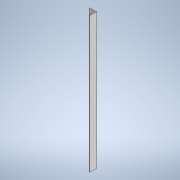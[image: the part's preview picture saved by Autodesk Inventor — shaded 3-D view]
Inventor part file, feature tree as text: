
AUTODESK INVENTOR PART (.ipt)
format: ipt  version: 2020.1 (Build 241239000, 239)  size: 97,792 bytes
history: native  units: mm
features: other x1, extrude x1, sketch x1
ambient origin geometry x8: Origin, YZ Plane, XZ Plane, XY Plane, X Axis, Y Axis, Z Axis, Center Point
bodies: Body1 (feature_tree)
feature tree (3):
  other  "Твердое тело1"
  extrude  "Выдавливание1"  Depth=5.0mm
  sketch  "Эскиз1"
